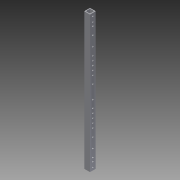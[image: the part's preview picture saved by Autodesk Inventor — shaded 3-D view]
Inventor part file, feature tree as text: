
AUTODESK INVENTOR PART (.ipt)
format: ipt  version: 2013 (Build 170138000, 138)  size: 195,072 bytes
history: native  units: in
note: dims shown in document units (in); Inventor stores cm internally (conversion verified against a paired STEP export)
features: reference x7, extrude x4, sketch x4
ambient origin geometry x8: Origin, YZ Plane, XZ Plane, XY Plane, X Axis, Y Axis, Z Axis, Center Point
bodies: Solid1 (feature_tree)
feature tree (15):
  extrude  "Extrusion1"  Depth=1.0in
  extrude  "Extrusion2"  Depth=24.0in TaperAngle=0.0deg
  extrude  "Extrusion3"  Depth=1.75in
  extrude  "Extrusion4"  Depth=1.75in
  sketch  "Sketch1"  dims[d0=1.0in d1=1.0in]
  sketch  "Sketch2"  dims[d2=0.125in d3=24.0in d4=0.0in]
  sketch  "Sketch3"  dims[d5=1.0in d6=0.0in d7=1.75in]
  reference  "Reference8"
  reference  "Reference9"
  reference  "Reference10"
  reference  "Reference11"
  reference  "Reference12"
  reference  "Reference13"
  reference  "Reference14"
  sketch  "Sketch4"  dims[d8=2.375in d9=1.75in d10=1.75in d11=0.26in d12=0.26in d13=0.26in d14=0.26in d15=0.26in d16=0.26in d17=0.26in d18=0.26in d19=1.0in d20=0.0in d21=2.375in d22=0.26in d23=0.26in d27=0.375in d28=0.375in d29=3.8722in d30=9.2907in d31=9.2907in d32=3.8722in d33=3.5in d34=0.26in d35=2.3622in d37=0.75in d38=0.3937in d40=1.0in d42=2.3622in d44=0.75in d45=0.3937in d47=1.0in d49=1.0in d50=0.0in]
